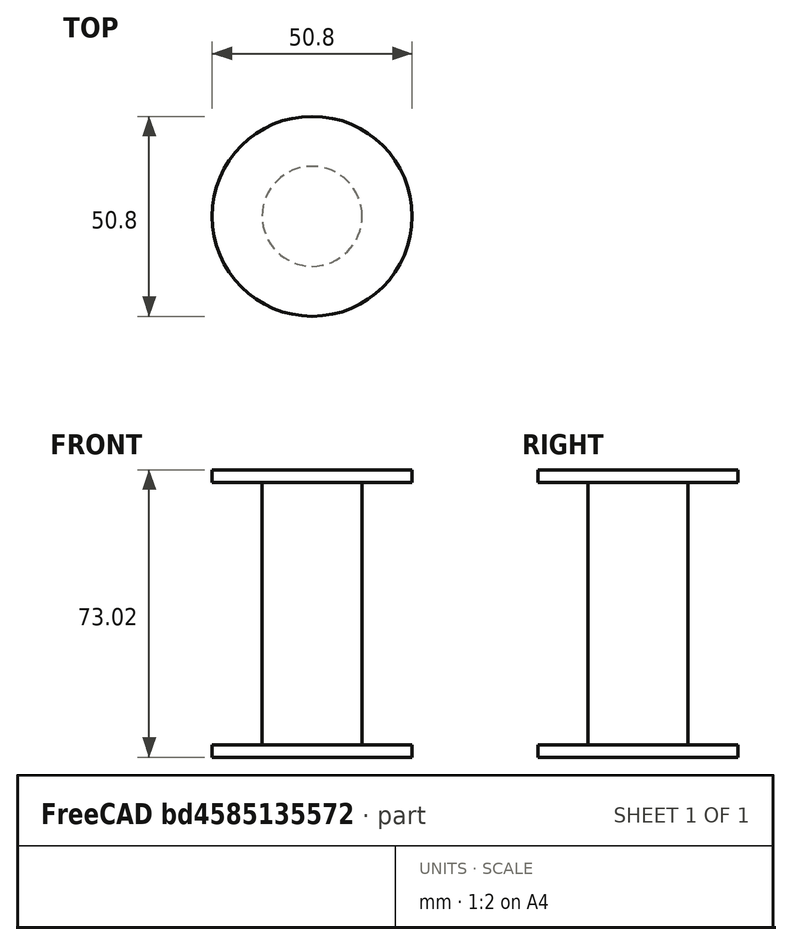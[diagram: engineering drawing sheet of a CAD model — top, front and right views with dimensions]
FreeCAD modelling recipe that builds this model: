
FCSTD DOCUMENT  (FreeCAD 0.16R6702 (Git))
Label: trackpin
License: All rights reserved
LicenseURL: http://en.wikipedia.org/wiki/All_rights_reserved
objects: App::FeaturePython×4, Part::Cylinder×3, Part::MultiFuse×1
note: 4 computed .brp shape members not serialized (recipe doc carries the construction recipe); baked Part::Feature solids carry a one-line shape summary decoded from their .brp

FEATURE [Part::Cylinder] Cylinder001
  Angle = 360
  Height = 69.85
  Radius = 12.7
FEATURE [Part::Cylinder] Cylinder003
  Angle = 360
  Height = 3.17
  Radius = 25.4
FEATURE [Part::Cylinder] Cylinder004
  Angle = 360
  Height = 3.17
  Placement = pos=(0,0,69.85) rot=(0,0,1;0rad)
  Radius = 25.4
FEATURE [App::FeaturePython] axialConstraint01  # a2plus constraint (typed FeaturePython)
  Object1 = Cylinder001
  Object2 = Cylinder004
  SubElement1 = Face1
  SubElement2 = Face1
  Type = axial
  directionConstraint = 0
  lockRotation = false
FEATURE [App::FeaturePython] planeConstraint01  # a2plus constraint (typed FeaturePython)
  Object1 = Cylinder001
  Object2 = Cylinder004
  SubElement1 = Face2
  SubElement2 = Face3
  Type = plane
  directionConstraint = 0
  offset = 0
FEATURE [App::FeaturePython] circularEdgeConstraint01  # a2plus constraint (typed FeaturePython)
  Object1 = Cylinder001
  Object2 = Cylinder004
  SubElement1 = Edge1
  SubElement2 = Edge3
  Type = circularEdge
  directionConstraint = 0
  lockRotation = false
  offset = 0
FEATURE [App::FeaturePython] planeConstraint02  # a2plus constraint (typed FeaturePython)
  Object1 = Cylinder001
  Object2 = Cylinder004
  SubElement1 = Face2
  SubElement2 = Face3
  Type = plane
  directionConstraint = 0
  offset = 0
FEATURE [Part::MultiFuse] Fusion
  Shapes = -> [Cylinder004,Cylinder003,Cylinder001]
